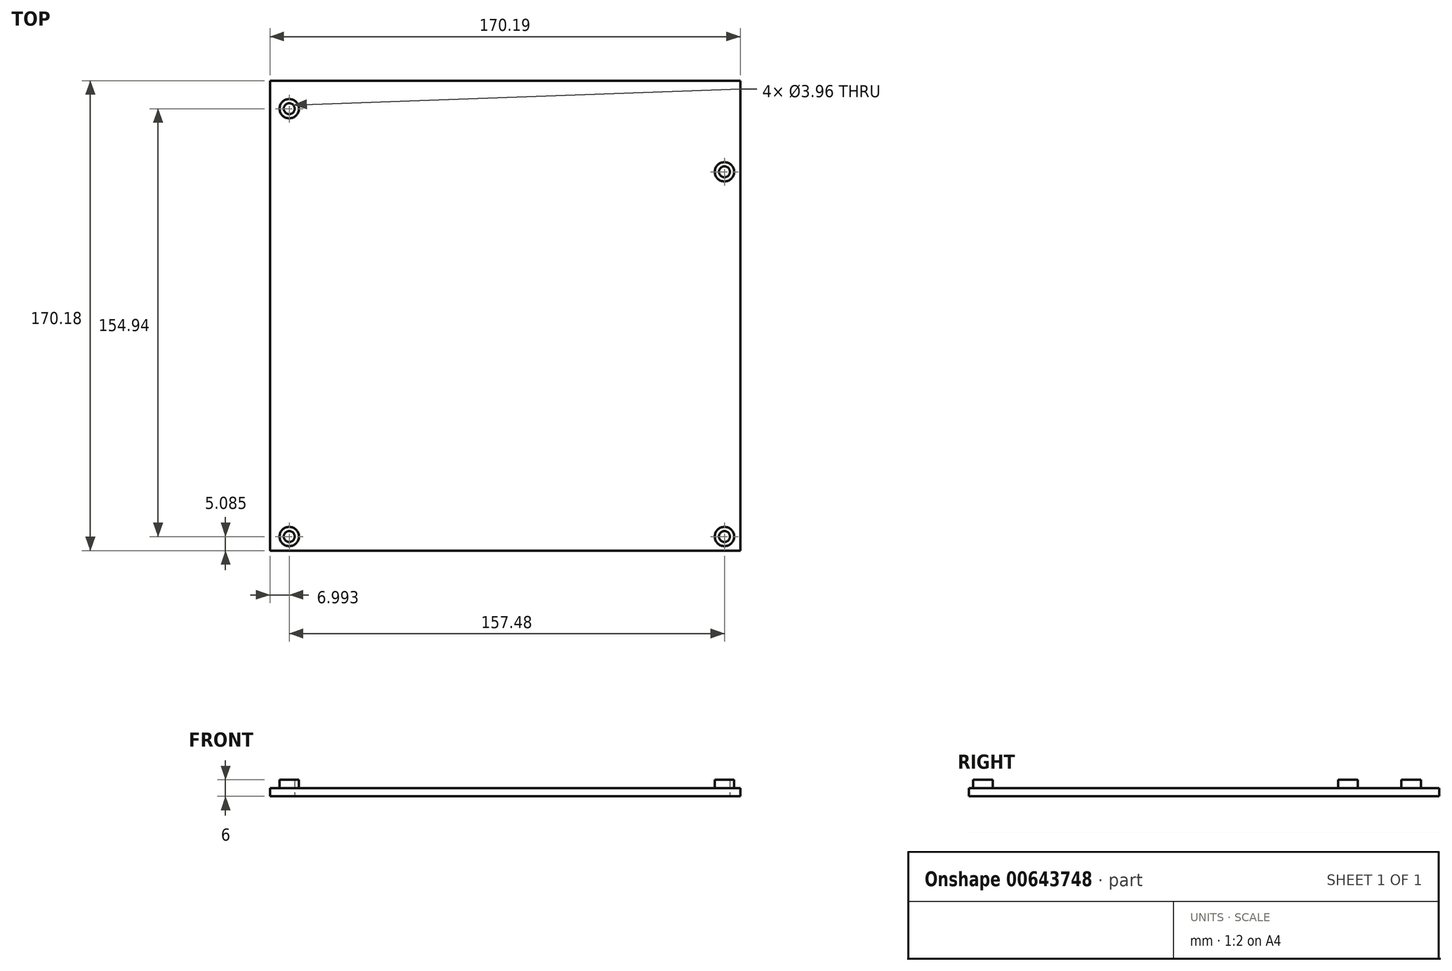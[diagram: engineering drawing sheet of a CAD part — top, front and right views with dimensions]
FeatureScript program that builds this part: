
annotation { "Feature Type Name" : "Feature", "Feature Type Description" : "" }
export const myFeature = defineFeature(function(context is Context, id is Id, definition is map)
    precondition{}
    {
        {
            var Q0;
            Q0=qCreatedBy(makeId("Top.planeOp"),FACE);
            var sketch = newSketch(context, id + "F0", { "sketchPlane" : qUnion([Q0])});
            skLineSegment(sketch, "E0.bottom", {"start": v(-88.04, -108.35) * mm, "end": v(82.15, -108.35) * mm});
            skLineSegment(sketch, "E0.top", {"start": v(-88.04, 61.83) * mm, "end": v(82.15, 61.83) * mm});
            skLineSegment(sketch, "E0.left", {"start": v(-88.04, -108.35) * mm, "end": v(-88.04, 61.83) * mm});
            skLineSegment(sketch, "E0.right", {"start": v(82.15, -108.35) * mm, "end": v(82.15, 61.83) * mm});
            skCircle(sketch, "E1", {"center": v(-81.05, -103.27) * mm, "radius": 1.98 * mm});
            skCircle(sketch, "E2", {"center": v(76.43, -103.27) * mm, "radius": 1.98 * mm});
            skCircle(sketch, "E3", {"center": v(-81.05, 51.67) * mm, "radius": 1.98 * mm});
            skCircle(sketch, "E4", {"center": v(76.43, 28.81) * mm, "radius": 1.98 * mm});
            skCircle(sketch, "E5", {"center": v(-81.05, 51.67) * mm, "radius": 3.5 * mm});
            skCircle(sketch, "E6", {"center": v(76.43, 28.81) * mm, "radius": 3.5 * mm});
            skCircle(sketch, "E7", {"center": v(76.43, -103.27) * mm, "radius": 3.5 * mm});
            skCircle(sketch, "E8", {"center": v(-81.05, -103.27) * mm, "radius": 3.5 * mm});
            skSolve(sketch);
        }
        {
            var Q0;
            Q0=makeQuery(id+"F0.imprint","IMPRINT",FACE,{"disambiguationData":[TD([[makeQuery(id+"F0.imprint","IMPRINT",EDGE,{"derivedFrom":sQuery(id+"F0.wireOp",EDGE,"E0.bottom")}),1.0]])]});
            extrude(context, id + "F1", {"entities" : qUnion([Q0]), "depth" : 3 * mm, "offsetDistance" : 25 * mm});
        }
        {
            var Q0;
            Q0=makeQuery(id+"F0.imprint","IMPRINT",FACE,{"disambiguationData":[TD([[makeQuery(id+"F0.imprint","IMPRINT",EDGE,{"derivedFrom":sQuery(id+"F0.wireOp",EDGE,"E2")}),-1.0]])]});
            var Q1;
            Q1=makeQuery(id+"F0.imprint","IMPRINT",FACE,{"disambiguationData":[TD([[makeQuery(id+"F0.imprint","IMPRINT",EDGE,{"derivedFrom":sQuery(id+"F0.wireOp",EDGE,"E1")}),-1.0]])]});
            var Q2;
            Q2=makeQuery(id+"F0.imprint","IMPRINT",FACE,{"disambiguationData":[TD([[makeQuery(id+"F0.imprint","IMPRINT",EDGE,{"derivedFrom":sQuery(id+"F0.wireOp",EDGE,"E3")}),-1.0]])]});
            var Q3;
            Q3=makeQuery(id+"F0.imprint","IMPRINT",FACE,{"disambiguationData":[TD([[makeQuery(id+"F0.imprint","IMPRINT",EDGE,{"derivedFrom":sQuery(id+"F0.wireOp",EDGE,"E4")}),-1.0]])]});
            extrude(context, id + "F2", {"entities" : qUnion([Q0, Q1, Q2, Q3]), "operationType" : NewBodyOperationType.ADD, "depth" : 6 * mm, "offsetDistance" : 25 * mm});
        }
    });
